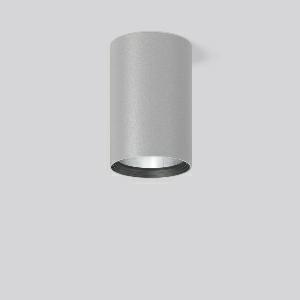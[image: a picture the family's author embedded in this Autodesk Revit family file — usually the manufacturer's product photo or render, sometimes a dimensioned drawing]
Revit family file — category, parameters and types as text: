
# Revit family: heledon_maxi_a_931217_004_3_76_5826
name_source: partatom
category: Lighting Fixtures
units: mm (PartAtom-declared; Revit-internal decimal feet)

## family parameters
Cut with Voids When Loaded = No
Host = Face
Light Source = No
Part Type = Normal
Room Calculation Point = No
Round Connector Dimension = Use Diameter
Shared = No

## types (1)
- HELEDON maxi A (1 x LED Modul 935, 3400 lm, 3500)
    Apparent Load = 25 VA
    Approval mark = CE
    CIE Flux Codes = 100 100 100 100 100
    Color Rendering = 92
    Color Temperature = 3500
    Default Elevation = 1800 mm
    Description = Series: HELEDON maxi
Cylindrical surface-mounted downlight. Housing: die-cast aluminium, powder-coated. Internal ceiling frame polycarbonate with bayonet mounting. Black plastic ring and recessed LED to prevent glare from the side. Optical assembly with reflector made of MIRO-Silver with 98% total light reflection for outstanding efficiency - can be changed without tools. Best colour rendering index Ra>90. Suitable for Ceiling mounting. Easy installation with a separate ceiling frame with bayonet mounting and plug connection. Driver integrated. Connected via plug-in connector. High quality converter without flickering and stroboscopic effect. The following accessories can be mounted without use of tools: interchangeable lenses, decorative glasses, honeycomb louvre, clear and frosted diffusers, white interchangeable plastic ring. 
Colour: silver
Diameter: 123 mm
Height: 183 mm
Lamp: LED
Socket: without socket
Colour temperature: 3500K
Colour rendering index (CRI): 92
System power: 25 W
Rated luminous flux: 3400 lm
Luminous efficiency: 136 lm/W
Control gear: Converter, dimmable, DALI
Protection class: I
Type of protection: IP 20
    Height = 183 mm
    Lamp = 1 x LED Modul 935
    Lamp Light Flux = 3400 lm
    Lamp count = 1
    Length = 123 mm
    Lifetime = 50000 h
    Luminous efficacy = 136 lm/W
    Manufacturer = RZB
    ModVariant = No
    Model = 931217.004.3.76
    Mounting Place = Ceiling
    Mounting Type = Surface mounted
    Number of Poles = 1
    OnlyDefault = Yes
    Power Factor = 1
    Product Name = HELEDON maxi A
    Product group = Surface mounted downlights
    ProductGroupID = 302
    Protection Class = Protection class I
    Protection Degree = IP 20
    RLX_Detail_Level = 1
    RLX_Emergency_Light_Flux = 0 lm
    RLX_Emergency_Type = 0
    RLX_Emergency_Type_DB = No
    RlxData = <blob elided: 99629 chars, md5=160bfa17>
    Socket = socket
    Standby Power = 0 W
    System Light Flux = 3400 lm
    System Power = 25 W
    Type Comments = Product without accessories
    Type Image = 931192.004.jpg
    URL = http://relux.com
    VarID = ---
    Voltage = 230 V
    Voltage Range = 220-240 V
    Weight = 0.00 kg
    Width = 0 mm  [stored 0 ft]

note: [stored X ft] marks values corroborated as IEEE doubles in the binary element streams (Revit-internal decimal feet)

## geometry (parser evidence)
native form markers: Blend x4, Sweep x12
no freeform markers — native parametric forms only
